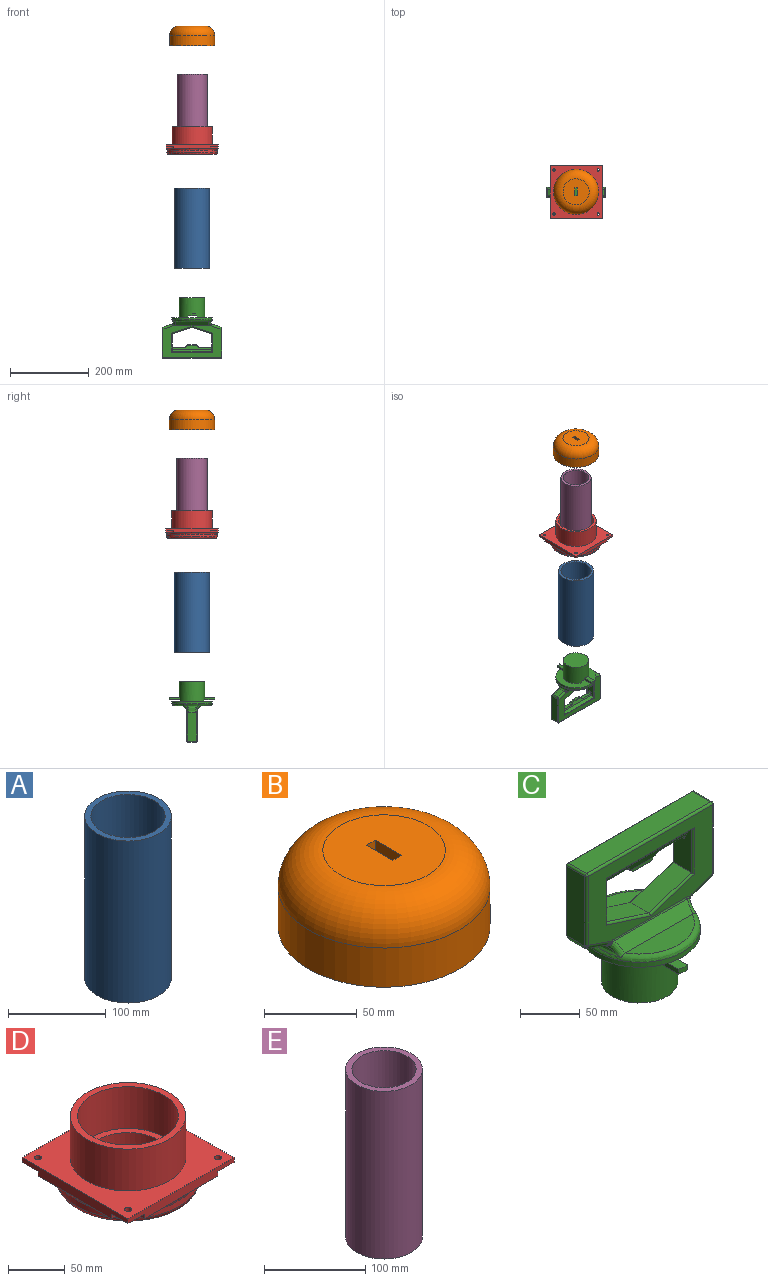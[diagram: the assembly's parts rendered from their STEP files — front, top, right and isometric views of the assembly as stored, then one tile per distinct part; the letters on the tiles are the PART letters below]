
ASSEMBLY  parts=5 mates=3
PART A: 4 faces, bbox 88.9x88.9x203.2 mm
  f0: cylinder r=38.1mm len=203.2mm, axis (0,0,-1), area 48643.9mm2, adj f2,f3
  f1: cylinder r=44.45mm len=203.2mm, axis (0,0,-1), area 56751.2mm2, adj f2,f3
  f2: plane 88.9x88.9mm, normal (0,0,1), area 1646.8mm2, adj f0,f1
  f3: plane 88.9x88.9mm, normal (0,0,-1), area 1646.8mm2, adj f0,f1
PART B: 10 faces, bbox 123.7x123.7x50 mm
  f0: plane 88.9x88.9mm, normal (0,0,-1), area 6074.5mm2, adj f5,f6,f7,f8,f9
  f1: plane 66.02x66.02mm, normal (0,0,1), area 3290.2mm2, adj f4,f6,f7,f8,f9
  f2: cylinder r=57.15mm len=114.3mm, axis (0,0,-1), area 9285.1mm2, adj f3,f4
  f3: plane 114.3x114.3mm, normal (0,0,-1), area 4053.7mm2, adj f2,f5
  f4: torus R=33.01mm, axis (0,0,1), area 11527mm2, adj f1,f2
  f5: cylinder r=44.45mm len=88.9mm, axis (0,0,-1), area 7093.9mm2, adj f0,f3
  f6: plane 24.6x6.6mm, normal (0,1,0), area 162.4mm2, adj f0,f1,f7,f9
  f7: plane 24.6x20.1mm, normal (1,0,0), area 494.5mm2, adj f0,f1,f6,f8
  f8: plane 24.6x6.6mm, normal (0,-1,0), area 162.4mm2, adj f0,f1,f7,f9
  f9: plane 24.6x20.1mm, normal (-1,0,0), area 494.5mm2, adj f0,f1,f6,f8
PART C: 100 faces, bbox 151.9x115.2x153.2 mm
  f0: cylinder r=32mm len=64.01mm, axis (0,0,1), area 9730.1mm2, adj f5,f88,f89,f91,f92,f93,f94,f96
  f1: plane 25.37x9.54mm, normal (0,0,-1), area 242.1mm2, adj f43,f46,f47,f48
  f2: plane 79.56x23.1mm, normal (0,0,1), area 1304.2mm2, adj f19,f20
  f3: plane 79.56x23.1mm, normal (0,0,1), area 1304.2mm2, adj f18,f20
  f4: cylinder r=50.8mm len=101.6mm, axis (0,0,1), area 1595.9mm2, adj f5,f20
  f5: plane 101.6x101.6mm, normal (0,0,-1), area 6256.9mm2, adj f0,f4,f97,f98
  f6: plane 50.37x21.4mm, normal (0.31,0,0.95), area 1132.1mm2, adj f7,f15,f62,f80
  f7: plane 43.57x21.4mm, normal (1,0,0), area 780.4mm2, adj f6,f23,f24,f46,f47,f49,f64,f79
  f8: plane 25.37x9.54mm, normal (0,0,-1), area 242.1mm2, adj f42,f46,f47,f49
  f9: plane 43.57x21.4mm, normal (-1,0,0), area 780.4mm2, adj f15,f23,f24,f46,f47,f48,f65,f83
  f10: plane 71.68x21.4mm, normal (-1,0,0), area 1533.9mm2, adj f35,f54,f55,f71,f72,f84
  f11: plane 21.27x15.42mm, normal (-0.33,0,-0.94), area 342.1mm2, adj f21,f34,f35,f36
  f12: plane 21.27x15.41mm, normal (0.33,0,-0.94), area 342.1mm2, adj f22,f27,f28,f29
  f13: plane 71.68x21.4mm, normal (1,0,0), area 1533.9mm2, adj f28,f51,f52,f68,f69,f86
  f14: plane 147.04x21.4mm, normal (0,0,1), area 3146.6mm2, adj f53,f70,f84,f86
  f15: plane 50.37x21.4mm, normal (-0.31,0,0.95), area 1132.1mm2, adj f6,f9,f63,f82
  f16: plane 147.04x80.68mm, normal (0,-1,0), area 5577.2mm2, adj f26,f27,f36,f37,f52,f53,f54,f58
  f17: plane 147.06x80.7mm, normal (0,1,0), area 5577.2mm2, adj f29,f30,f33,f34,f69,f70,f71,f75
  f18: plane 86.25x9.53mm, normal (0,-0.71,0.71), area 1102.5mm2, adj f3,f20,f25,f38,f59
  f19: plane 86.25x9.53mm, normal (0,0.71,0.71), area 1102.5mm2, adj f2,f20,f31,f32,f76
  f20: torus R=45.8mm, axis (0,0,1), area 1998.1mm2, adj f2,f3,f4,f18,f19,f21,f22,f25
  f21: bspline ~52.85x10.86mm, area 260.1mm2, adj f11,f20,f32,f33,f37,f38
  f22: bspline ~48.84x9.01mm, area 260.2mm2, adj f12,f20,f25,f26,f30,f31
  f23: plane 103.57x5.88mm, normal (0,0.71,-0.71), area 840.4mm2, adj f7,f9,f46,f79,f81,f83
  f24: plane 102.03x6mm, normal (0,-0.71,-0.71), area 838.3mm2, adj f7,f9,f47,f64,f65,f66
  f25: bspline ~17.51x14.72mm, area 101mm2, adj f18,f20,f22,f57,f58
  f26: bspline ~7.6x7.2mm, area 23.7mm2, adj f16,f22,f27,f57
  f27: cylinder r=5mm len=25.9mm, axis (-0.94,0,-0.33), area 190.6mm2, adj f12,f16,f26,f50,f51
  f28: cylinder r=5mm len=21.07mm, axis (0,1,0), area 112.7mm2, adj f12,f13,f50,f67
  f29: cylinder r=5mm len=25.9mm, axis (0.94,0,0.33), area 190.6mm2, adj f12,f17,f30,f67,f68
  f30: bspline ~7.6x7.2mm, area 23.7mm2, adj f17,f22,f29,f74
  f31: bspline ~17.71x14.89mm, area 101.2mm2, adj f19,f20,f22,f74,f75
  f32: bspline ~17.51x14.72mm, area 99.7mm2, adj f19,f20,f21,f77,f78
  f33: bspline ~7.6x7.2mm, area 23.7mm2, adj f17,f21,f34,f78
  f34: cylinder r=5mm len=25.9mm, axis (0.94,0,-0.33), area 190.6mm2, adj f11,f17,f33,f72,f73
  f35: cylinder r=5mm len=21.07mm, axis (0,1,0), area 112.7mm2, adj f10,f11,f56,f73
  f36: cylinder r=5mm len=25.9mm, axis (-0.94,0,0.33), area 190.6mm2, adj f11,f16,f37,f55,f56
  f37: bspline ~7.6x7.2mm, area 23.7mm2, adj f16,f21,f36,f61
  f38: bspline ~17.71x14.89mm, area 101mm2, adj f18,f20,f21,f60,f61
  f39: plane 27.75x3mm, normal (0,1,0), area 72.2mm2, adj f41,f44,f45,f46
  f40: plane 27.75x3mm, normal (0,-1,0), area 72.2mm2, adj f41,f44,f45,f47
  f41: plane 20.4x5.4mm, normal (0,0,-1), area 110.2mm2, adj f39,f40,f44,f45
  f42: cylinder r=5mm len=9.54mm, axis (0,-1,0), area 54mm2, adj f8,f45,f46,f47
  f43: cylinder r=5mm len=9.54mm, axis (0,1,0), area 54mm2, adj f1,f44,f46,f47
  f44: plane 6.23x4.9mm, normal (0.63,0,-0.77), area 34.8mm2, adj f39,f40,f41,f43,f46,f47
  f45: plane 6.23x4.9mm, normal (-0.63,0,-0.77), area 34.8mm2, adj f39,f40,f41,f42,f46,f47
  f46: plane 101.61x9.41mm, normal (0,0.92,-0.38), area 569.9mm2, adj f1,f7,f8,f9,f23,f39,f42,f43
  f47: plane 101.61x9.41mm, normal (0,-0.92,-0.38), area 569.9mm2, adj f1,f7,f8,f9,f24,f40,f42,f43
  f48: cylinder r=5mm len=9.54mm, axis (0,-1,0), area 58.7mm2, adj f1,f9,f46,f47
  f49: cylinder r=5mm len=9.54mm, axis (0,1,0), area 58.7mm2, adj f7,f8,f46,f47
  f50: bspline ~5.09x4.83mm, area 7.2mm2, adj f27,f28,f51
  f51: bspline ~3.04x2.33mm, area 4.4mm2, adj f13,f27,f50,f52
  f52: cylinder r=2mm len=70.64mm, axis (0,0,-1), area 221.9mm2, adj f13,f16,f51,f87
  f53: cylinder r=2mm len=147.04mm, axis (1,0,0), area 461.9mm2, adj f14,f16,f85,f87
  f54: cylinder r=2mm len=70.64mm, axis (0,0,1), area 221.9mm2, adj f10,f16,f55,f85
  f55: bspline ~3.04x2.33mm, area 4.4mm2, adj f10,f36,f54,f56
  f56: bspline ~5.09x4.83mm, area 7.2mm2, adj f35,f36,f55
  f57: bspline ~5.45x5.14mm, area 5.3mm2, adj f25,f26,f58
  f58: bspline ~4.94x2.93mm, area 4.3mm2, adj f16,f25,f57,f59
  f59: cylinder r=2mm len=86.2mm, axis (-1,0,0), area 135.4mm2, adj f16,f18,f58,f60
  f60: bspline ~4.94x2.93mm, area 4.3mm2, adj f16,f38,f59,f61
  f61: bspline ~5.13x4.81mm, area 9mm2, adj f37,f38,f60
  f62: cylinder r=2mm len=52.98mm, axis (0.95,0,-0.31), area 169.5mm2, adj f6,f16,f63,f64
  f63: cylinder r=2mm len=52.98mm, axis (0.95,0,0.31), area 169.5mm2, adj f15,f16,f62,f65
  f64: cylinder r=2mm len=47.85mm, axis (0,0,-1), area 143.6mm2, adj f7,f16,f24,f62,f66
  f65: cylinder r=2mm len=47.85mm, axis (0,0,1), area 143.6mm2, adj f9,f16,f24,f63,f66
  f66: cylinder r=2mm len=104.74mm, axis (1,0,0), area 162.3mm2, adj f16,f24,f64,f65
  f67: bspline ~4.72x4.72mm, area 6.5mm2, adj f28,f29,f68
  f68: bspline ~2.17x2mm, area 3.8mm2, adj f13,f29,f67,f69
  f69: plane 72.33x2.28mm, normal (0.71,0.71,0), area 202mm2, adj f13,f17,f68,f70,f86
  f70: plane 150.15x2.28mm, normal (0,0.71,0.71), area 420.3mm2, adj f14,f17,f69,f71,f84,f86
  f71: plane 72.33x2.28mm, normal (-0.71,0.71,0), area 202mm2, adj f10,f17,f70,f72,f84
  f72: bspline ~2.17x2mm, area 3.8mm2, adj f10,f34,f71,f73
  f73: bspline ~4.72x4.72mm, area 6.5mm2, adj f34,f35,f72
  f74: bspline ~5.15x4.81mm, area 8.9mm2, adj f30,f31,f75
  f75: bspline ~3.22x2.14mm, area 4.1mm2, adj f17,f31,f74,f76
  f76: plane 86.2x1.41mm, normal (0,0.92,0.38), area 131.9mm2, adj f17,f19,f75,f77
  f77: bspline ~3.22x2.13mm, area 4.1mm2, adj f17,f32,f76,f78
  f78: bspline ~5.18x4.81mm, area 5.3mm2, adj f32,f33,f77
  f79: plane 47.85x2mm, normal (0.71,0.71,0), area 128.5mm2, adj f7,f17,f23,f80,f81
  f80: plane 52.37x18.27mm, normal (0.22,0.71,0.67), area 152.6mm2, adj f6,f17,f79,f82
  f81: plane 104.74x1.41mm, normal (0,0.92,-0.38), area 159.4mm2, adj f17,f23,f79,f83
  f82: plane 52.37x18.27mm, normal (-0.22,0.71,0.67), area 152.6mm2, adj f15,f17,f80,f83
  f83: plane 47.85x2mm, normal (-0.71,0.71,0), area 128.5mm2, adj f9,f17,f23,f81,f82
  f84: cylinder r=2mm len=21.99mm, axis (0,-1,0), area 68.2mm2, adj f10,f14,f70,f71,f85
  f85: sphere r=2mm, area 6.3mm2, adj f53,f54,f84
  f86: cylinder r=2mm len=21.99mm, axis (0,1,0), area 68.2mm2, adj f13,f14,f69,f70,f87
  f87: sphere r=2mm, area 6.3mm2, adj f52,f53,f86
  f88: plane 64.01x64.01mm, normal (0,0,-1), area 3217.8mm2, adj f0
  f89: plane 25.15x5mm, normal (1,0,0), area 125.7mm2, adj f0,f90,f92,f99
  f90: cylinder r=57.15mm len=10mm, axis (0,0,1), area 50.3mm2, adj f89,f91,f92,f99
  f91: plane 25.87x5mm, normal (-1,0,0), area 129.3mm2, adj f0,f90,f92,f99
  f92: plane 26.75x10mm, normal (0,0,-1), area 253.8mm2, adj f0,f89,f90,f91
  f93: plane 25.87x5mm, normal (1,0,0), area 129.3mm2, adj f0,f95,f96,f99
  f94: plane 25.15x5mm, normal (-1,0,0), area 125.7mm2, adj f0,f95,f96,f99
  f95: cylinder r=57.15mm len=10mm, axis (0,0,1), area 50.3mm2, adj f93,f94,f96,f99
  f96: plane 26.75x10mm, normal (0,0,-1), area 253.8mm2, adj f0,f93,f94,f95
  f97: plane 59.5x5mm, normal (-1,0,0), area 297.5mm2, adj f0,f5,f99
  f98: plane 60.8x5mm, normal (1,0,0), area 304mm2, adj f0,f5,f99
  f99: plane 114.3x21.8mm, normal (0,0,1), area 1875mm2, adj f0,f89,f90,f91,f93,f94,f95,f97
PART D: 93 faces, bbox 150.5x150.5x71.1 mm
  f0: plane 132x132mm, normal (0,0,1), area 9203.6mm2, adj f6,f7,f9,f10,f11,f12,f17,f18
  f1: plane 88.9x88.9mm, normal (0,0,1), area 1646.8mm2, adj f15,f92
  f2: plane 123x123mm, normal (0,0,-1), area 6533.4mm2, adj f15,f16,f20,f25,f28,f29,f31,f32
  f3: plane 47.66x47.66mm, normal (0,0,-1), area 353.5mm2, adj f6,f7,f39,f40,f41,f58
  f4: plane 47.66x47.66mm, normal (0,0,-1), area 353.5mm2, adj f6,f17,f44,f45,f46,f54
  f5: plane 47.66x47.66mm, normal (0,0,-1), area 353.5mm2, adj f17,f18,f35,f36,f37,f53
  f6: plane 132.21x10.21mm, normal (0,1,0), area 1120mm2, adj f0,f3,f4,f7,f17,f41,f42,f43
  f7: plane 132.21x10.21mm, normal (1,0,0), area 1120mm2, adj f0,f3,f6,f8,f18,f39,f42,f47
  f8: plane 47.66x47.66mm, normal (0,0,-1), area 353.5mm2, adj f7,f18,f48,f49,f50,f57
  f9: cylinder r=3mm len=6mm, axis (0,0,1), area 94.2mm2, adj f0,f47
  f10: cylinder r=3mm len=6mm, axis (0,0,1), area 94.2mm2, adj f0,f43
  f11: cylinder r=3mm len=6mm, axis (0,0,1), area 94.2mm2, adj f0,f42
  f12: cylinder r=3mm len=6mm, axis (0,0,1), area 94.2mm2, adj f0,f38
  f13: plane 56.27x47.15mm, normal (0,0,1), area 1233.1mm2, adj f16,f26,f27,f28
  f14: plane 56.27x47.15mm, normal (0,0,1), area 1233.1mm2, adj f15,f21,f23,f31
  f15: cylinder r=38.1mm len=76.2mm, axis (0,0,-1), area 4438mm2, adj f1,f2,f14,f16,f20,f21,f22,f24
  f16: cylinder r=38.1mm len=36.76mm, axis (0,0,-1), area 248.6mm2, adj f2,f13,f15,f28
  f17: plane 132.21x10.21mm, normal (-1,0,0), area 1120mm2, adj f0,f4,f5,f6,f18,f35,f38,f43
  f18: plane 132.21x10.21mm, normal (0,-1,0), area 1120mm2, adj f0,f5,f7,f8,f17,f37,f38,f47
  f19: cylinder r=63.5mm len=127mm, axis (0,0,1), area 2365.6mm2, adj f51,f52,f53,f54,f55,f56,f57,f58
  f20: plane 19.05x15mm, normal (-1,0,0), area 285.7mm2, adj f2,f15,f22,f23,f32
  f21: plane 19.05x10mm, normal (0,1,0), area 190.5mm2, adj f14,f15,f22,f23
  f22: plane 57.15x57.15mm, normal (0,0,-1), area 1425.1mm2, adj f15,f20,f21,f23
  f23: cylinder r=57.15mm len=57.15mm, axis (0,0,-1), area 897.7mm2, adj f14,f20,f21,f22,f33
  f24: plane 57.15x57.15mm, normal (0,0,-1), area 1425.1mm2, adj f15,f25,f26,f27
  f25: plane 19.05x15mm, normal (1,0,0), area 285.7mm2, adj f2,f15,f24,f27,f29
  f26: plane 19.05x10mm, normal (0,-1,0), area 190.5mm2, adj f13,f15,f24,f27
  f27: cylinder r=57.15mm len=57.15mm, axis (0,0,-1), area 897.7mm2, adj f13,f24,f25,f26,f30
  f28: plane 20.39x5mm, normal (-1,0,0), area 101.9mm2, adj f2,f13,f16,f29,f30
  f29: plane 10x5mm, normal (0,1,0), area 50mm2, adj f2,f25,f28,f30
  f30: plane 10x0.88mm, normal (0,0,-1), area 2.9mm2, adj f27,f28,f29
  f31: plane 20.39x5mm, normal (1,0,0), area 101.9mm2, adj f2,f14,f15,f32,f33
  f32: plane 10x5mm, normal (0,-1,0), area 50mm2, adj f2,f20,f31,f33
  f33: plane 10x0.88mm, normal (0,0,-1), area 2.9mm2, adj f23,f31,f32
  f34: cone r=63.5mm half-angle=45deg, axis (0,0,1), area 293.9mm2, adj f2,f51
  f35: plane 10x5mm, normal (0,-1,0), area 50mm2, adj f5,f17,f36,f38
  f36: cylinder r=10mm len=10mm, axis (0,0,-1), area 78.5mm2, adj f5,f35,f37,f38
  f37: plane 10x5mm, normal (-1,0,0), area 50mm2, adj f5,f18,f36,f38
  f38: plane 20x20mm, normal (0,0,-1), area 350.3mm2, adj f12,f17,f18,f35,f36,f37
  f39: plane 10x5mm, normal (0,1,0), area 50mm2, adj f3,f7,f40,f42
  f40: cylinder r=10mm len=10mm, axis (0,0,-1), area 78.5mm2, adj f3,f39,f41,f42
  f41: plane 10x5mm, normal (1,0,0), area 50mm2, adj f3,f6,f40,f42
  f42: plane 20x20mm, normal (0,0,-1), area 350.3mm2, adj f6,f7,f11,f39,f40,f41
  f43: plane 20x20mm, normal (0,0,-1), area 350.3mm2, adj f6,f10,f17,f44,f45,f46
  f44: cylinder r=10mm len=10mm, axis (0,0,-1), area 78.5mm2, adj f4,f43,f45,f46
  f45: plane 10x5mm, normal (0,1,0), area 50mm2, adj f4,f17,f43,f44
  f46: plane 10x5mm, normal (-1,0,0), area 50mm2, adj f4,f6,f43,f44
  f47: plane 20x20mm, normal (0,0,-1), area 350.3mm2, adj f7,f9,f18,f48,f49,f50
  f48: cylinder r=10mm len=10mm, axis (0,0,-1), area 78.5mm2, adj f8,f47,f49,f50
  f49: plane 10x5mm, normal (0,-1,0), area 50mm2, adj f7,f8,f47,f48
  f50: plane 10x5mm, normal (1,0,0), area 50mm2, adj f8,f18,f47,f48
  f51: torus R=58.5mm, axis (0,0,-1), area 1554.5mm2, adj f19,f34
  f52: bspline ~39.22x5.51mm, area 214.9mm2, adj f17,f19,f53,f54
  f53: torus R=68.5mm, axis (0,0,1), area 527.8mm2, adj f5,f19,f52,f55
  f54: torus R=68.5mm, axis (0,0,1), area 527.8mm2, adj f4,f19,f52,f56
  f55: bspline ~39.22x5.51mm, area 214.9mm2, adj f18,f19,f53,f57
  f56: bspline ~39.22x5.51mm, area 214.9mm2, adj f6,f19,f54,f58
  f57: torus R=68.5mm, axis (0,0,1), area 527.8mm2, adj f8,f19,f55,f59
  f58: torus R=68.5mm, axis (0,0,1), area 527.8mm2, adj f3,f19,f56,f59
  f59: bspline ~39.22x5.51mm, area 214.9mm2, adj f7,f19,f57,f58
  f60: plane 1.63x1.5mm, normal (0.87,-0.5,0), area 2.8mm2, adj f2,f61,f66,f79
  f61: cylinder r=46.33mm len=40.12mm, axis (0,0,-1), area 72.8mm2, adj f2,f60,f62,f77
  f62: plane 3.76x1.5mm, normal (0,-1,0), area 5.6mm2, adj f2,f61,f63,f76
  f63: cylinder r=42.57mm len=36.87mm, axis (0,0,-1), area 66.9mm2, adj f2,f62,f64,f78
  f64: plane 1.63x1.5mm, normal (0.87,-0.5,0), area 2.8mm2, adj f2,f63,f65,f80
  f65: plane 6.51x3.76mm, normal (-0.87,-0.5,0), area 11.3mm2, adj f2,f64,f66,f82
  f66: plane 7.52x1.5mm, normal (0,1,0), area 11.3mm2, adj f2,f60,f65,f81
  f67: plane 39.75x27mm, normal (0,0,-1), area 88.9mm2, adj f76,f77,f78,f79,f80,f81,f82
  f68: cylinder r=42.57mm len=36.87mm, axis (0,0,-1), area 66.9mm2, adj f2,f69,f74,f87
  f69: plane 1.63x1.5mm, normal (-0.87,0.5,0), area 2.8mm2, adj f2,f68,f70,f89
  f70: plane 6.51x3.76mm, normal (0.87,0.5,0), area 11.3mm2, adj f2,f69,f71,f88
  f71: plane 7.52x1.5mm, normal (0,-1,0), area 11.3mm2, adj f2,f70,f72,f86
  f72: plane 1.63x1.5mm, normal (-0.87,0.5,0), area 2.8mm2, adj f2,f71,f73,f84
  f73: cylinder r=46.33mm len=40.12mm, axis (0,0,-1), area 72.8mm2, adj f2,f72,f74,f83
  f74: plane 3.76x1.5mm, normal (0,1,0), area 5.6mm2, adj f2,f68,f73,f85
  f75: plane 39.75x27mm, normal (0,0,-1), area 88.9mm2, adj f83,f84,f85,f86,f87,f88,f89
  f76: cylinder r=1mm len=3.76mm, axis (1,0,0), area 4.3mm2, adj f62,f67,f77,f78
  f77: torus R=45.33mm, axis (0,0,-1), area 75.6mm2, adj f61,f67,f76,f79
  f78: torus R=43.57mm, axis (0,0,-1), area 70.6mm2, adj f63,f67,f76,f80
  f79: cylinder r=1mm len=3mm, axis (0.5,0.87,0), area 2.4mm2, adj f60,f67,f77,f81
  f80: cylinder r=1mm len=2.98mm, axis (0.5,0.87,0), area 2.4mm2, adj f64,f67,f78,f82
  f81: cylinder r=1mm len=7.52mm, axis (-1,0,0), area 9.1mm2, adj f66,f67,f79,f82
  f82: cylinder r=1mm len=7.01mm, axis (0.5,-0.87,0), area 9.1mm2, adj f65,f67,f80,f81
  f83: torus R=45.33mm, axis (0,0,-1), area 75.6mm2, adj f73,f75,f84,f85
  f84: cylinder r=1mm len=3mm, axis (-0.5,-0.87,0), area 2.4mm2, adj f72,f75,f83,f86
  f85: cylinder r=1mm len=3.76mm, axis (-1,0,0), area 4.3mm2, adj f74,f75,f83,f87
  f86: cylinder r=1mm len=7.52mm, axis (1,0,0), area 9.1mm2, adj f71,f75,f84,f88
  f87: torus R=43.57mm, axis (0,0,-1), area 70.6mm2, adj f68,f75,f85,f89
  f88: cylinder r=1mm len=7.01mm, axis (-0.5,0.87,0), area 9.1mm2, adj f70,f75,f86,f89
  f89: cylinder r=1mm len=2.98mm, axis (-0.5,-0.87,0), area 2.4mm2, adj f69,f75,f87,f88
  f90: cylinder r=50.8mm len=101.6mm, axis (0,0,-1), area 14363.4mm2, adj f0,f91
  f91: plane 101.6x101.6mm, normal (0,0,1), area 1900.2mm2, adj f90,f92
  f92: cylinder r=44.45mm len=88.9mm, axis (0,0,-1), area 12567.9mm2, adj f1,f91
PART E: 4 faces, bbox 76.2x76.2x203.2 mm
  f0: cylinder r=31.75mm len=203.2mm, axis (0,0,-1), area 40536.6mm2, adj f2,f3
  f1: cylinder r=38.1mm len=203.2mm, axis (0,0,-1), area 48643.9mm2, adj f2,f3
  f2: plane 76.2x76.2mm, normal (0,0,1), area 1393.4mm2, adj f0,f1
  f3: plane 76.2x76.2mm, normal (0,0,-1), area 1393.4mm2, adj f0,f1
PLACE A t=(-26.14,-17.55,-299.19)mm
PLACE B t=(-26.14,-17.55,264.61)mm
PLACE C rot(axis=(1,0,0),180deg) t=(-26.33,-17.55,-433.62)mm
PLACE D t=(-26.14,-17.55,9.81)mm
PLACE E t=(-26.14,-17.55,-10.62)mm
MATE slider A.f1 <-> D.f19  axis (0,0,-1) through (-26.14,-17.55,-299.19)mm
MATE slider C.f5 <-> E.f0  axis (0,0,1) through (-26.14,-17.55,-423.62)mm
MATE slider B.f5 <-> A.f0  axis (0,0,-1) through (-26.14,-17.55,290.01)mm
